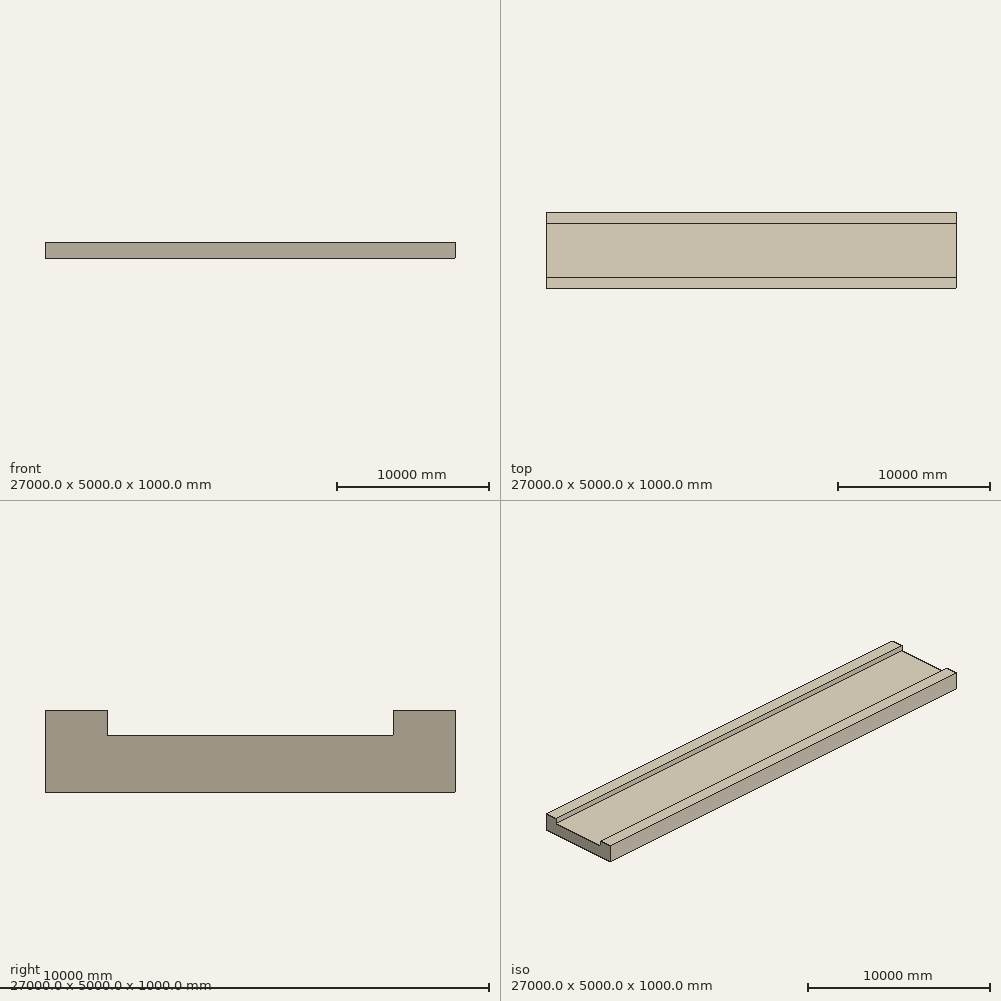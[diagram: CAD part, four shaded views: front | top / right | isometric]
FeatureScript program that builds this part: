
annotation { "Feature Type Name" : "Feature", "Feature Type Description" : "" }
export const myFeature = defineFeature(function(context is Context, id is Id, definition is map)
    precondition{}
    {
        {
            var Q0;
            Q0=qCreatedBy(makeId("Top.planeOp"),FACE);
            var sketch = newSketch(context, id + "F0", { "sketchPlane" : qUnion([Q0])});
            skLineSegment(sketch, "E0.bottom", {"start": v(-13500, 2500) * mm, "end": v(13500, 2500) * mm});
            skLineSegment(sketch, "E0.top", {"start": v(-13500, -2500) * mm, "end": v(13500, -2500) * mm});
            skLineSegment(sketch, "E0.left", {"start": v(-13500, 2500) * mm, "end": v(-13500, -2500) * mm});
            skLineSegment(sketch, "E0.right", {"start": v(13500, 2500) * mm, "end": v(13500, -2500) * mm});
            skPoint(sketch, "E0.middle", {"position": v(0, 0) * mm});
            skLineSegment(sketch, "E1", {"start": v(-13500, 1750) * mm, "end": v(13500, 1750) * mm});
            skLineSegment(sketch, "E2", {"start": v(13500, 0) * mm, "end": v(-13500, 0) * mm, "construction": true});
            skLineSegment(sketch, "E3.MirrorCS", {"start": v(-13500, -1750) * mm, "end": v(13500, -1750) * mm});
            skSolve(sketch);
        }
        {
            var Q0;
            {var subQ0=sQuery(id+"F0.wireOp",EDGE,"E0.bottom");Q0=makeQuery(id+"F0.imprint","IMPRINT",FACE,{"disambiguationData":[TD([[makeQuery(id+"F0.imprint","IMPRINT",EDGE,{"derivedFrom":subQ0}),-1.0]])]});}
            var Q1;
            {var subQ0=sQuery(id+"F0.wireOp",EDGE,"E1");Q1=makeQuery(id+"F0.imprint","IMPRINT",FACE,{"disambiguationData":[TD([[makeQuery(id+"F0.imprint","IMPRINT",EDGE,{"derivedFrom":subQ0}),-1.0]])]});}
            var Q2;
            {var subQ0=sQuery(id+"F0.wireOp",EDGE,"E0.top");Q2=makeQuery(id+"F0.imprint","IMPRINT",FACE,{"disambiguationData":[TD([[makeQuery(id+"F0.imprint","IMPRINT",EDGE,{"derivedFrom":subQ0}),1.0]])]});}
            extrude(context, id + "F1", {"entities" : qUnion([Q0, Q1, Q2]), "depth" : 700 * mm});
        }
        {
            var Q0;
            {var subQ0=sQuery(id+"F0.wireOp",EDGE,"E0.top");Q0=makeQuery(id+"F0.imprint","IMPRINT",FACE,{"disambiguationData":[TD([[makeQuery(id+"F0.imprint","IMPRINT",EDGE,{"derivedFrom":subQ0}),1.0]])]});}
            var Q1;
            {var subQ0=sQuery(id+"F0.wireOp",EDGE,"E0.bottom");Q1=makeQuery(id+"F0.imprint","IMPRINT",FACE,{"disambiguationData":[TD([[makeQuery(id+"F0.imprint","IMPRINT",EDGE,{"derivedFrom":subQ0}),-1.0]])]});}
            extrude(context, id + "F2", {"entities" : qUnion([Q0, Q1]), "operationType" : NewBodyOperationType.ADD, "depth" : 1000 * mm});
        }
    });
